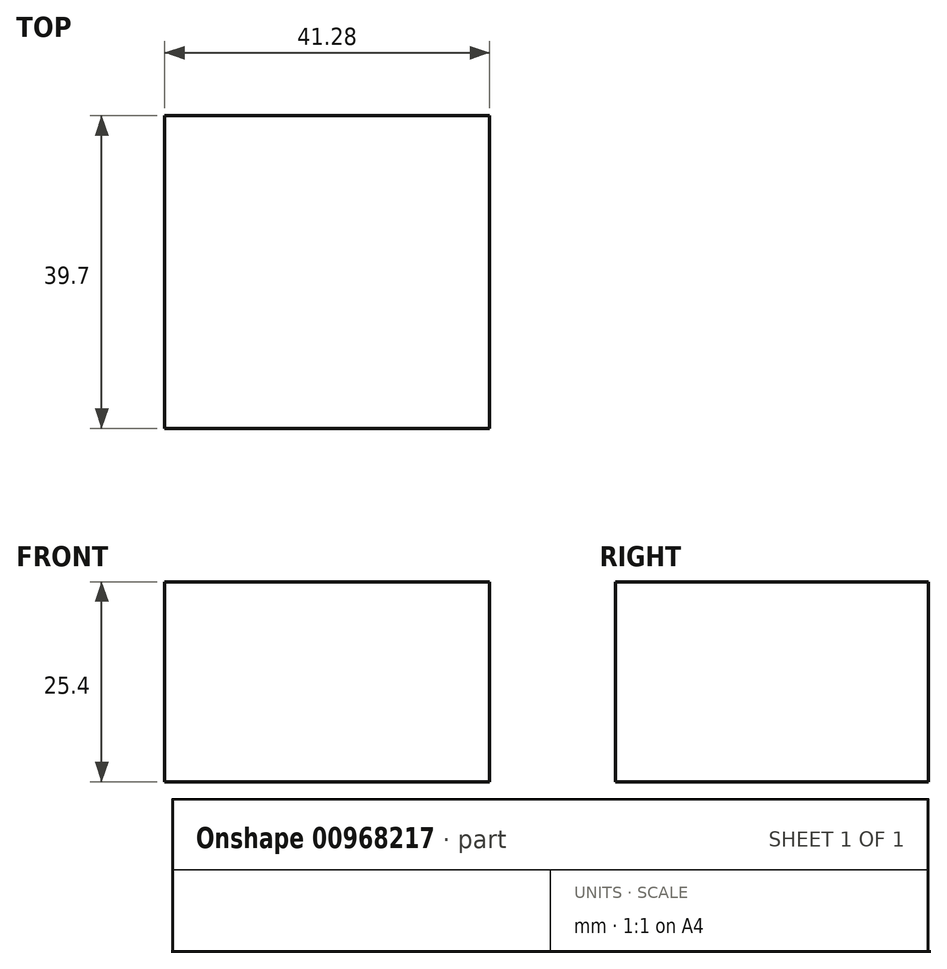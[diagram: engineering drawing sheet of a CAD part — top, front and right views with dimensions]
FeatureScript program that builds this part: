
annotation { "Feature Type Name" : "Feature", "Feature Type Description" : "" }
export const myFeature = defineFeature(function(context is Context, id is Id, definition is map)
    precondition{}
    {
        {
            var Q0;
            Q0=qCreatedBy(makeId("Top.planeOp"),FACE);
            var sketch = newSketch(context, id + "F0", { "sketchPlane" : qUnion([Q0])});
            skLineSegment(sketch, "E0.bottom", {"start": v(20.64, -19.85) * mm, "end": v(-20.64, -19.85) * mm});
            skLineSegment(sketch, "E0.top", {"start": v(20.64, 19.85) * mm, "end": v(-20.64, 19.85) * mm});
            skLineSegment(sketch, "E0.left", {"start": v(20.64, -19.85) * mm, "end": v(20.64, 19.85) * mm});
            skLineSegment(sketch, "E0.right", {"start": v(-20.64, -19.85) * mm, "end": v(-20.64, 19.85) * mm});
            skPoint(sketch, "E0.middle", {"position": v(0, 0) * mm});
            skSolve(sketch);
        }
        {
            var Q0;
            Q0=makeQuery(id+"F0.imprint","IMPRINT",FACE,{"disambiguationData":[TD([[makeQuery(id+"F0.imprint","IMPRINT",EDGE,{"derivedFrom":sQuery(id+"F0.wireOp",EDGE,"E0.bottom")}),-1.0]])]});
            extrude(context, id + "F1", {"entities" : qUnion([Q0]), "depth" : 25.4 * mm, "offsetDistance" : 25.4 * mm});
        }
    });
